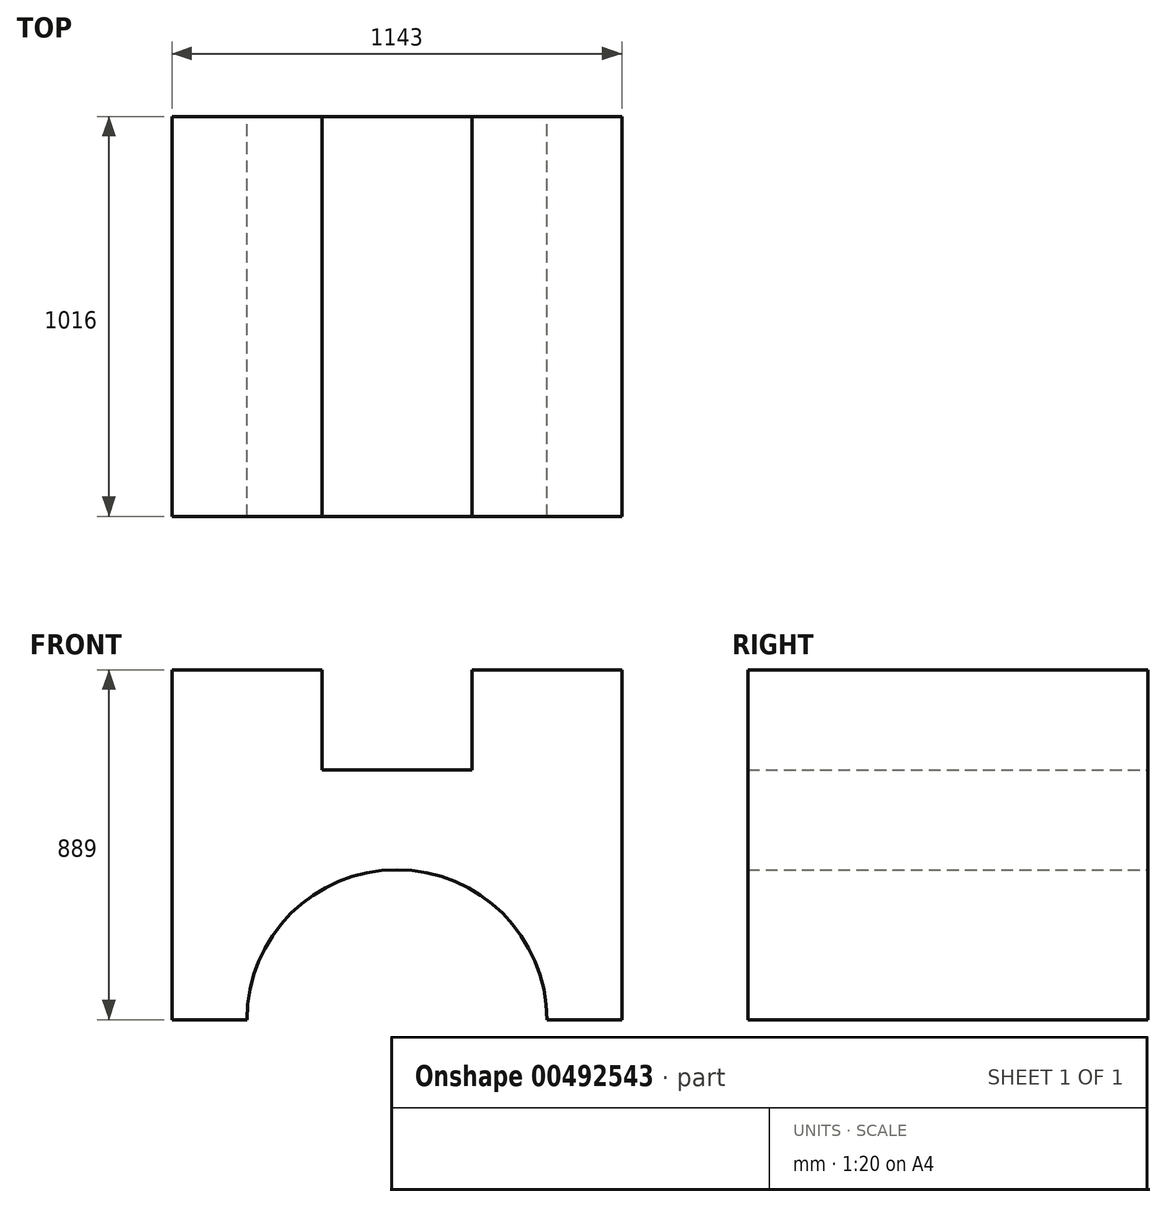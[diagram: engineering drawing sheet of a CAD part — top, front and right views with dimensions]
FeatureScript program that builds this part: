
annotation { "Feature Type Name" : "Feature", "Feature Type Description" : "" }
export const myFeature = defineFeature(function(context is Context, id is Id, definition is map)
    precondition{}
    {
        {
            var Q0;
            Q0=qCreatedBy(makeId("Front.planeOp"),FACE);
            var sketch = newSketch(context, id + "F0", { "sketchPlane" : qUnion([Q0])});
            skLineSegment(sketch, "E0.bottom", {"start": v(0, 0) * mm, "end": v(190.5, 0) * mm});
            skLineSegment(sketch, "E0.top", {"start": v(0, 889) * mm, "end": v(1143, 889) * mm});
            skLineSegment(sketch, "E0.left", {"start": v(0, 0) * mm, "end": v(0, 889) * mm});
            skLineSegment(sketch, "E0.right", {"start": v(1143, 0) * mm, "end": v(1143, 889) * mm});
            skArc(sketch, "E1", {"start": v(952.5, 0) * mm, "mid": v(571.5, 381) * mm, "end": v(190.5, 0) * mm});
            skLineSegment(sketch, "E2.trimOffspring", {"start": v(952.5, 0) * mm, "end": v(1143, 0) * mm});
            skLineSegment(sketch, "E3", {"start": v(381, 889) * mm, "end": v(381, 635) * mm});
            skLineSegment(sketch, "E4", {"start": v(381, 635) * mm, "end": v(762, 635) * mm});
            skLineSegment(sketch, "E5", {"start": v(762, 635) * mm, "end": v(762, 889) * mm});
            skSolve(sketch);
        }
        {
            var Q0;
            Q0=makeQuery(id+"F0.imprint","IMPRINT",FACE,{"disambiguationData":[TD([[makeQuery(id+"F0.imprint","IMPRINT",EDGE,{"derivedFrom":sQuery(id+"F0.wireOp",EDGE,"E0.bottom")}),1.0]])]});
            extrude(context, id + "F1", {"entities" : qUnion([Q0]), "depth" : 1016 * mm});
        }
    });
